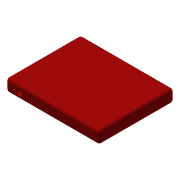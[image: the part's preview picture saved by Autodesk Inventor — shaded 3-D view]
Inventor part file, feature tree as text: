
AUTODESK INVENTOR PART (.ipt)
format: ipt  version: 2016 (Build 200138000, 138)  size: 113,664 bytes
history: native  units: mm
features: hole x2, extrude x1, mirror x1, fillet x1, sketch x1
ambient origin geometry x8: Origin, YZ Plane, XZ Plane, XY Plane, X Axis, Y Axis, Z Axis, Center Point
bodies: Volumenkörper1 (feature_tree)
feature tree (6):
  extrude  "Extrusion1"  Depth=2.0mm
  hole  "Bohrung1"  [1 undecoded]
  mirror  "Spiegeln1"
  hole  "Bohrung2"  [1 undecoded]
  fillet  "Rundung2"  [1 undecoded]
  sketch  "Skizze1"  dims[d0=75.0mm d1=60.0mm d2=10.0mm d3=0.0mm d13=5.0mm d14=10.0mm d15=6.0mm d16=6.0mm d17=4.0mm d18=2.0mm d19=90.0deg d20=10.0mm d21=20.594885mm d22=5.0mm d23=3.0mm d24=2.459mm d25=6.0mm d26=4.0mm d27=2.0mm d28=90.0deg d29=8.0mm d30=20.594885mm d36=2.0mm]
note: 3 required parameter values undecoded (feature->parameter linkage not recoverable at this tier; creation-order binding heuristic only, values carry confidence <= 0.55)
